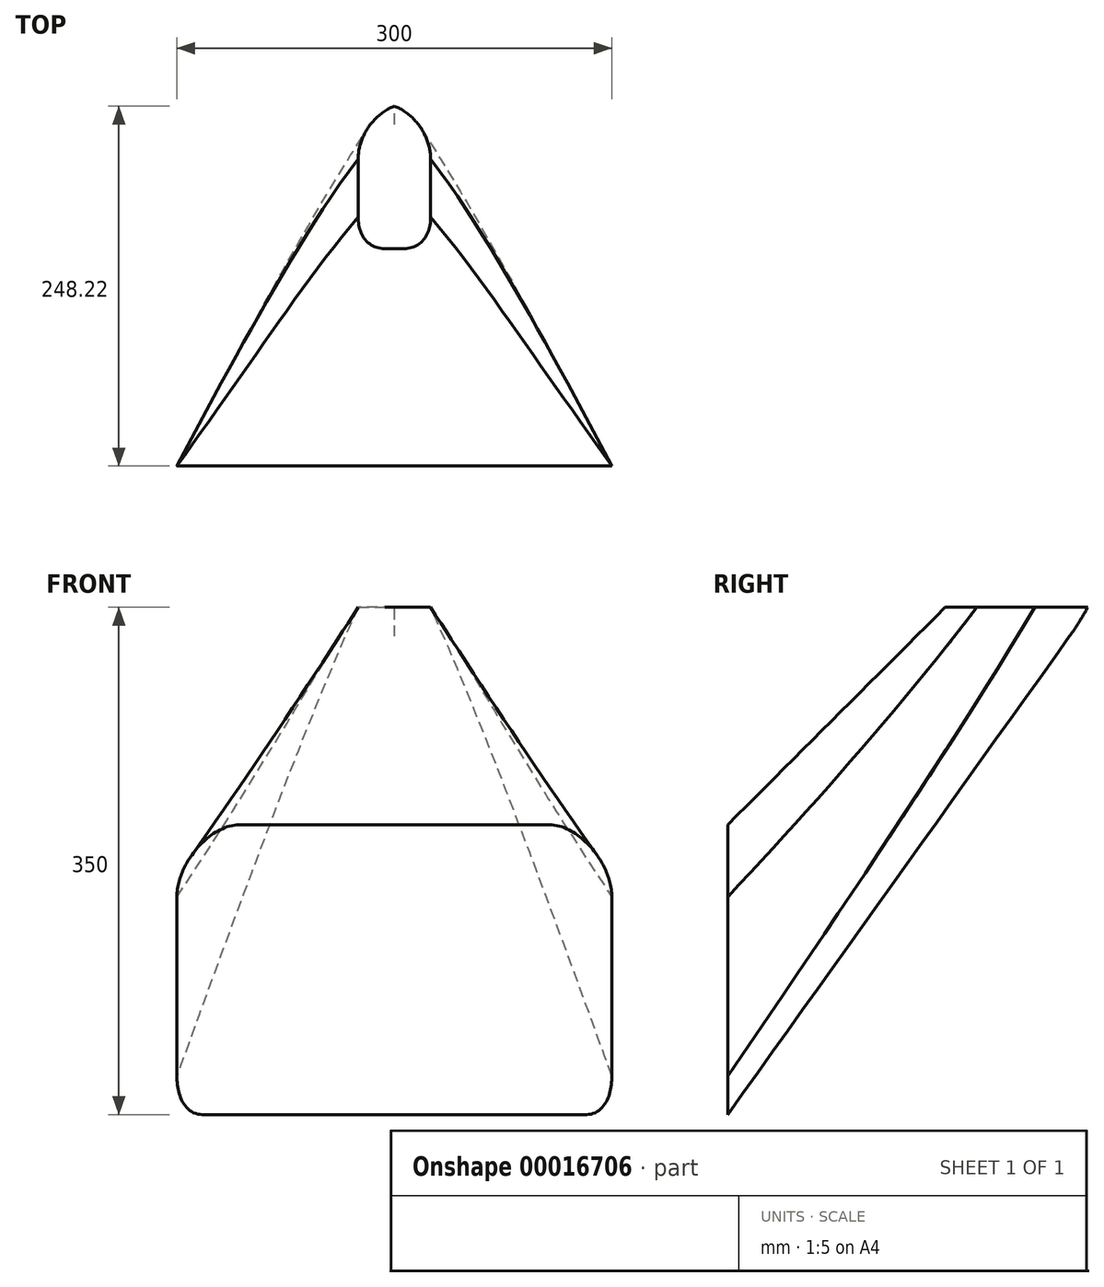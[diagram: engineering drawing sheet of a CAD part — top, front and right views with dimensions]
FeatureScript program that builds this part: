
annotation { "Feature Type Name" : "Feature", "Feature Type Description" : "" }
export const myFeature = defineFeature(function(context is Context, id is Id, definition is map)
    precondition{}
    {
        {
            var Q0;
            Q0=qCreatedBy(makeId("Top.planeOp"),FACE);
            cPlane(context, id + "F0", {"entities" : qUnion([Q0]), "cplaneType" : CPlaneType.OFFSET, "offset" : 250 * mm, "width" : 150 * mm, "height" : 150 * mm});
        }
        {
            var Q0;
            Q0=qCreatedBy(makeId("Front.planeOp"),FACE);
            var sketch = newSketch(context, id + "F1", { "sketchPlane" : qUnion([Q0])});
            skLineSegment(sketch, "E0.bottom", {"start": v(-150, 100) * mm, "end": v(150, 100) * mm});
            skLineSegment(sketch, "E0.top", {"start": v(-150, -100) * mm, "end": v(150, -100) * mm});
            skLineSegment(sketch, "E0.left", {"start": v(-150, 100) * mm, "end": v(-150, -100) * mm});
            skLineSegment(sketch, "E0.right", {"start": v(150, 100) * mm, "end": v(150, -100) * mm});
            skSolve(sketch);
        }
        {
            var Q0;
            Q0=qCreatedBy(id+"F0.planeOp",FACE);
            var sketch = newSketch(context, id + "F2", { "sketchPlane" : qUnion([Q0])});
            skLineSegment(sketch, "E1.bottom", {"start": v(-25, 250) * mm, "end": v(25, 250) * mm});
            skLineSegment(sketch, "E1.top", {"start": v(-25, 150) * mm, "end": v(25, 150) * mm});
            skLineSegment(sketch, "E1.left", {"start": v(-25, 250) * mm, "end": v(-25, 150) * mm});
            skLineSegment(sketch, "E1.right", {"start": v(25, 250) * mm, "end": v(25, 150) * mm});
            skSolve(sketch);
        }
        {
            var Q0;
            Q0=makeQuery(id+"F1.imprint","IMPRINT",FACE,{"disambiguationData":[TD([[makeQuery(id+"F1.imprint","IMPRINT",EDGE,{"derivedFrom":sQuery(id+"F1.wireOp",EDGE,"E0.bottom")}),-1.0]])]});
            var Q1;
            Q1=makeQuery(id+"F2.imprint","IMPRINT",FACE,{"disambiguationData":[TD([[makeQuery(id+"F2.imprint","IMPRINT",EDGE,{"derivedFrom":sQuery(id+"F2.wireOp",EDGE,"E1.bottom")}),-1.0]])]});
            loft(context, id + "F3", {"sheetProfilesArray" : [{ "sheetProfileEntities" : qUnion([Q0]) }, { "sheetProfileEntities" : qUnion([Q1]) }]});
        }
        {
            var Q0;
            Q0=makeQuery(id+"F3.opLoft","SWEPT_EDGE",EDGE,{"disambiguationData":[OSD([sQuery(id+"F1.wireOp",EDGE,"E0.bottom"),sQuery(id+"F1.wireOp",EDGE,"E0.right"),sQuery(id+"F2.wireOp",EDGE,"E1.top"),sQuery(id+"F2.wireOp",EDGE,"E1.right")])]});
            var Q1;
            Q1=makeQuery(id+"F3.opLoft","SWEPT_EDGE",EDGE,{"disambiguationData":[OSD([sQuery(id+"F1.wireOp",EDGE,"E0.bottom"),sQuery(id+"F1.wireOp",EDGE,"E0.left"),sQuery(id+"F2.wireOp",EDGE,"E1.top"),sQuery(id+"F2.wireOp",EDGE,"E1.left")])]});
            var Q2;
            Q2=makeQuery(id+"F3.opLoft","SWEPT_EDGE",EDGE,{"disambiguationData":[OSD([sQuery(id+"F1.wireOp",EDGE,"E0.top"),sQuery(id+"F1.wireOp",EDGE,"E0.right"),sQuery(id+"F2.wireOp",EDGE,"E1.bottom"),sQuery(id+"F2.wireOp",EDGE,"E1.right")])]});
            var Q3;
            Q3=makeQuery(id+"F3.opLoft","SWEPT_EDGE",EDGE,{"disambiguationData":[OSD([sQuery(id+"F1.wireOp",EDGE,"E0.top"),sQuery(id+"F1.wireOp",EDGE,"E0.left"),sQuery(id+"F2.wireOp",EDGE,"E1.bottom"),sQuery(id+"F2.wireOp",EDGE,"E1.left")])]});
            fillet(context, id + "F4", {"entities" : qUnion([Q0, Q1, Q2, Q3]), "radius" : 25 * mm, "allowEdgeOverflow" : false});
        }
    });
